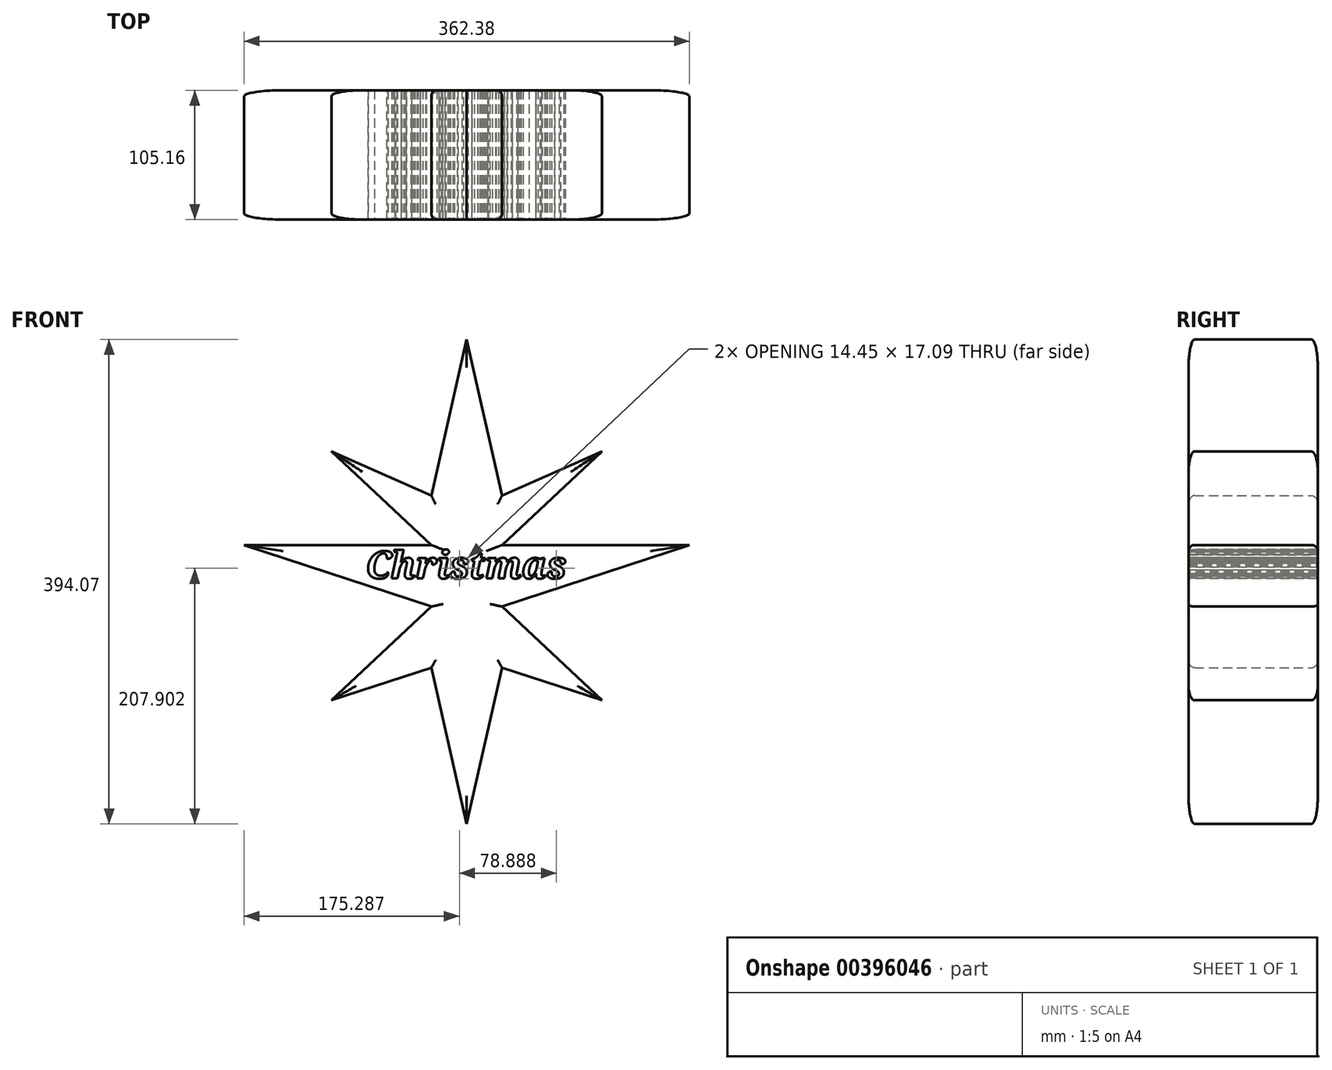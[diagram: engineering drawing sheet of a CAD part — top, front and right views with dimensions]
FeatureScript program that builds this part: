
annotation { "Feature Type Name" : "Feature", "Feature Type Description" : "" }
export const myFeature = defineFeature(function(context is Context, id is Id, definition is map)
    precondition{}
    {
        {
            var Q0;
            Q0=qCreatedBy(makeId("Front.planeOp"),FACE);
            var sketch = newSketch(context, id + "F0", { "sketchPlane" : qUnion([Q0])});
            skLineSegment(sketch, "E0", {"start": v(0, -226.88) * mm, "end": v(28.79, -99.88) * mm});
            skLineSegment(sketch, "E1", {"start": v(0, 167.19) * mm, "end": v(28.79, 40.19) * mm});
            skLineSegment(sketch, "E2", {"start": v(110.07, 76.2) * mm, "end": v(28.79, 0) * mm});
            skLineSegment(sketch, "E3", {"start": v(28.79, 0) * mm, "end": v(181.19, 0) * mm});
            skLineSegment(sketch, "E4", {"start": v(181.19, 0) * mm, "end": v(28.79, -50.12) * mm});
            skLineSegment(sketch, "E5.MirrorCS", {"start": v(0, 167.19) * mm, "end": v(-28.79, 40.19) * mm});
            skLineSegment(sketch, "E6.MirrorCS", {"start": v(-110.07, 76.2) * mm, "end": v(-28.79, 0) * mm});
            skLineSegment(sketch, "E7.MirrorCS", {"start": v(-28.79, 0) * mm, "end": v(-181.19, 0) * mm});
            skLineSegment(sketch, "E8.MirrorCS", {"start": v(-181.19, 0) * mm, "end": v(-28.79, -50.12) * mm});
            skLineSegment(sketch, "E9.MirrorCS", {"start": v(0, -226.88) * mm, "end": v(-28.79, -99.88) * mm});
            skLineSegment(sketch, "E10", {"start": v(28.79, -50.12) * mm, "end": v(110.07, -126.32) * mm});
            skLineSegment(sketch, "E11", {"start": v(110.07, -126.32) * mm, "end": v(28.79, -99.88) * mm});
            skLineSegment(sketch, "E12.MirrorCS", {"start": v(-110.07, -126.32) * mm, "end": v(-28.79, -99.88) * mm});
            skLineSegment(sketch, "E13.MirrorCS", {"start": v(-28.79, -50.12) * mm, "end": v(-110.07, -126.32) * mm});
            skLineSegment(sketch, "E14", {"start": v(-110.07, 76.2) * mm, "end": v(-28.79, 40.19) * mm});
            skLineSegment(sketch, "E15", {"start": v(28.79, 40.19) * mm, "end": v(110.07, 76.2) * mm});
            skSolve(sketch);
        }
        {
            var Q0;
            Q0=makeQuery(id+"F0.imprint","IMPRINT",FACE,{"disambiguationData":[TD([[makeQuery(id+"F0.imprint","IMPRINT",EDGE,{"derivedFrom":sQuery(id+"F0.wireOp",EDGE,"E0")}),1.0]])]});
            extrude(context, id + "F1", {"entities" : qUnion([Q0]), "depth" : 105.16 * mm});
        }
        {
            var Q0;
            Q0=makeQuery(id+"F1.opExtrude","CAP_FACE",FACE,{"disambiguationData":[OSD([sQuery(id+"F0.wireOp",EDGE,"E0"),sQuery(id+"F0.wireOp",EDGE,"E1"),sQuery(id+"F0.wireOp",EDGE,"C7HNz2aB-Yq8G-TduF-HsH4-OGhsupfJDwES"),sQuery(id+"F0.wireOp",EDGE,"E2"),sQuery(id+"F0.wireOp",EDGE,"trXxRECX-r7Vr-pvho-EPSv-4FOTPgYPuLjS"),sQuery(id+"F0.wireOp",EDGE,"hdwZvc65-AONW-gbYW-mDWK-Ff14jxQ0028O"),sQuery(id+"F0.wireOp",EDGE,"E3"),sQuery(id+"F0.wireOp",EDGE,"E4"),sQuery(id+"F0.wireOp",EDGE,"E5.MirrorCS"),sQuery(id+"F0.wireOp",EDGE,"06443c9d-8307-46b8-94de-ad076418fb930.MirrorCS"),sQuery(id+"F0.wireOp",EDGE,"E6.MirrorCS"),sQuery(id+"F0.wireOp",EDGE,"E7.MirrorCS"),sQuery(id+"F0.wireOp",EDGE,"E8.MirrorCS"),sQuery(id+"F0.wireOp",EDGE,"ba576363-b06c-4133-9d12-97047d3321ce0.MirrorCS"),sQuery(id+"F0.wireOp",EDGE,"4232ac8c-d644-47e5-8bf9-27e102cd50600.MirrorCS"),sQuery(id+"F0.wireOp",EDGE,"E9.MirrorCS")])],"isStart":false});
            var Q1;
            Q1=makeQuery(id+"F1.opExtrude","CAP_FACE",FACE,{"disambiguationData":[OSD([sQuery(id+"F0.wireOp",EDGE,"E0"),sQuery(id+"F0.wireOp",EDGE,"E1"),sQuery(id+"F0.wireOp",EDGE,"C7HNz2aB-Yq8G-TduF-HsH4-OGhsupfJDwES"),sQuery(id+"F0.wireOp",EDGE,"E2"),sQuery(id+"F0.wireOp",EDGE,"trXxRECX-r7Vr-pvho-EPSv-4FOTPgYPuLjS"),sQuery(id+"F0.wireOp",EDGE,"hdwZvc65-AONW-gbYW-mDWK-Ff14jxQ0028O"),sQuery(id+"F0.wireOp",EDGE,"E3"),sQuery(id+"F0.wireOp",EDGE,"E4"),sQuery(id+"F0.wireOp",EDGE,"E5.MirrorCS"),sQuery(id+"F0.wireOp",EDGE,"06443c9d-8307-46b8-94de-ad076418fb930.MirrorCS"),sQuery(id+"F0.wireOp",EDGE,"E6.MirrorCS"),sQuery(id+"F0.wireOp",EDGE,"E7.MirrorCS"),sQuery(id+"F0.wireOp",EDGE,"E8.MirrorCS"),sQuery(id+"F0.wireOp",EDGE,"ba576363-b06c-4133-9d12-97047d3321ce0.MirrorCS"),sQuery(id+"F0.wireOp",EDGE,"4232ac8c-d644-47e5-8bf9-27e102cd50600.MirrorCS"),sQuery(id+"F0.wireOp",EDGE,"E9.MirrorCS")])],"isStart":true});
            fillet(context, id + "F2", {"entities" : qUnion([Q0, Q1]), "radius" : 5.08 * mm, "tangentPropagation" : true, "allowEdgeOverflow" : false});
        }
        {
            var Q0;
            Q0=makeQuery(id+"F1.opExtrude","CAP_FACE",FACE,{"disambiguationData":[OSD([sQuery(id+"F0.wireOp",EDGE,"E0"),sQuery(id+"F0.wireOp",EDGE,"E1"),sQuery(id+"F0.wireOp",EDGE,"E2"),sQuery(id+"F0.wireOp",EDGE,"E3"),sQuery(id+"F0.wireOp",EDGE,"E4"),sQuery(id+"F0.wireOp",EDGE,"E5.MirrorCS"),sQuery(id+"F0.wireOp",EDGE,"E6.MirrorCS"),sQuery(id+"F0.wireOp",EDGE,"E7.MirrorCS"),sQuery(id+"F0.wireOp",EDGE,"E8.MirrorCS"),sQuery(id+"F0.wireOp",EDGE,"E9.MirrorCS"),sQuery(id+"F0.wireOp",EDGE,"E10"),sQuery(id+"F0.wireOp",EDGE,"E11"),sQuery(id+"F0.wireOp",EDGE,"E12.MirrorCS"),sQuery(id+"F0.wireOp",EDGE,"E13.MirrorCS"),sQuery(id+"F0.wireOp",EDGE,"E14"),sQuery(id+"F0.wireOp",EDGE,"E15")])],"isStart":false});
            var sketch = newSketch(context, id + "F3", { "sketchPlane" : qUnion([Q0])});
            skText(sketch, "E16", { "text": "Christmas", "fontName": "NotoSerif-BoldItalic.ttf"});
            const initialGuessF3  = {"E16": [-0.08218, -0.02722, 1, 0, 0.02214]};
            skSetInitialGuess(sketch, initialGuessF3);
            skSolve(sketch);
        }
        {
            var Q0;
            Q0 = qSketchRegion(id + "F3", true);
            extrude(context, id + "F4", {"entities" : qUnion([Q0]), "operationType" : NewBodyOperationType.REMOVE, "endBound" : BoundingType.THROUGH_ALL, "oppositeDirection" : true, "depth" : 25.4 * mm});
        }
    });
